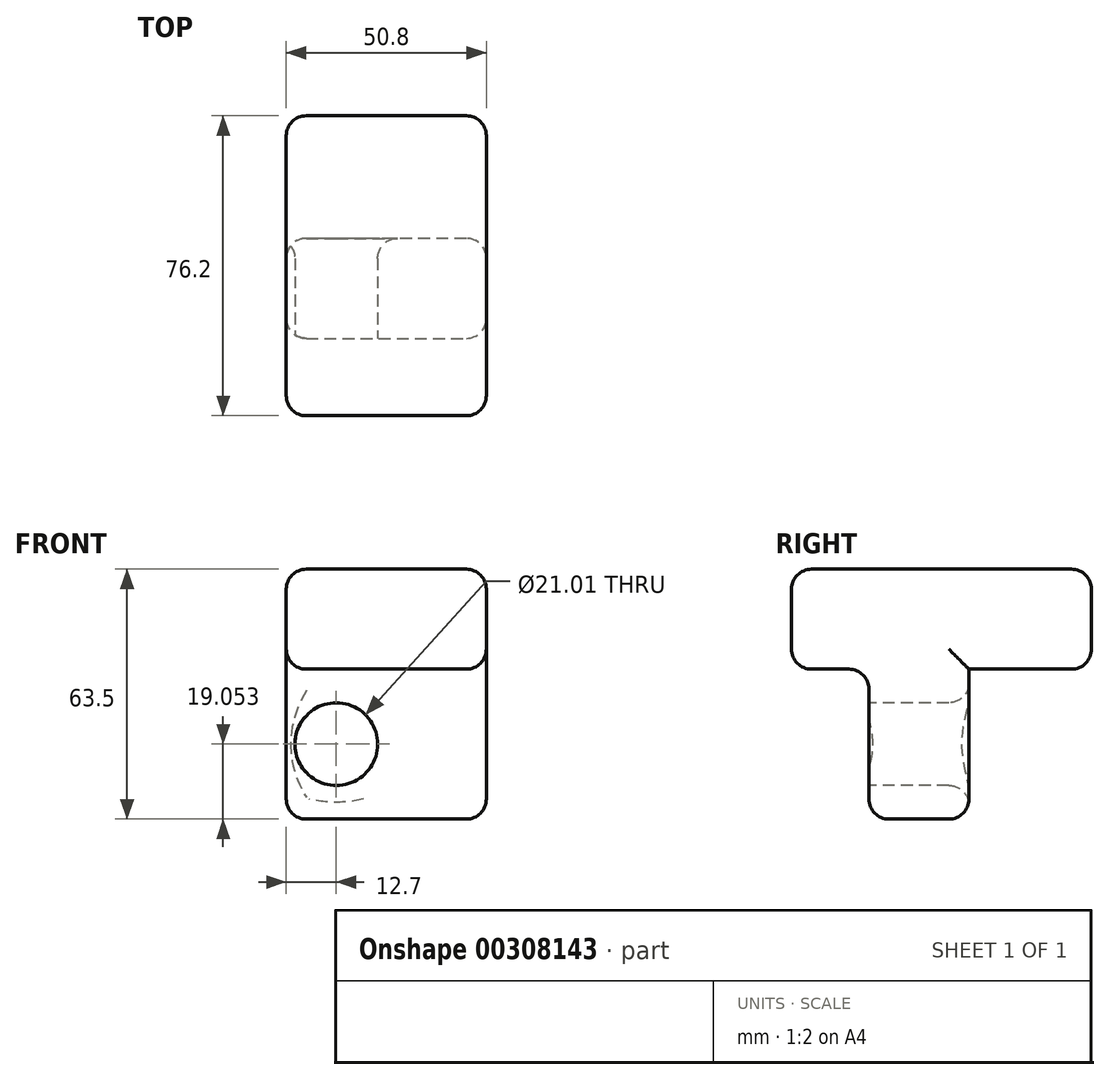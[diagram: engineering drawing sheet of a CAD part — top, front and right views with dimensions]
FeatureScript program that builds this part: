
annotation { "Feature Type Name" : "Feature", "Feature Type Description" : "" }
export const myFeature = defineFeature(function(context is Context, id is Id, definition is map)
    precondition{}
    {
        {
            var Q0;
            Q0=qCreatedBy(makeId("Front.planeOp"),FACE);
            var sketch = newSketch(context, id + "F0", { "sketchPlane" : qUnion([Q0])});
            skLineSegment(sketch, "E0", {"start": v(0, 47.5) * mm, "end": v(25.4, 47.5) * mm});
            skLineSegment(sketch, "E1", {"start": v(25.4, 47.5) * mm, "end": v(25.4, 22.1) * mm});
            skLineSegment(sketch, "E2", {"start": v(0, 22.1) * mm, "end": v(0, 47.5) * mm});
            skLineSegment(sketch, "E3", {"start": v(25.4, 22.1) * mm, "end": v(0, 22.1) * mm});
            skSolve(sketch);
        }
        {
            var Q0;
            Q0=makeQuery(id+"F0.imprint","IMPRINT",FACE,{"disambiguationData":[TD([[makeQuery(id+"F0.imprint","IMPRINT",EDGE,{"derivedFrom":sQuery(id+"F0.wireOp",EDGE,"E0")}),-1.0]])]});
            extrude(context, id + "F1", {"entities" : qUnion([Q0]), "depth" : 76.2 * mm});
        }
        {
            var Q0;
            Q0=makeQuery(id+"F1.opExtrude","SWEPT_FACE",FACE,{"disambiguationData":[OSD([sQuery(id+"F0.wireOp",EDGE,"E3")])]});
            var sketch = newSketch(context, id + "F2", { "sketchPlane" : qUnion([Q0])});
            skLineSegment(sketch, "E4", {"start": v(0, 56.54) * mm, "end": v(25.4, 56.54) * mm});
            skLineSegment(sketch, "E5", {"start": v(25.4, 56.54) * mm, "end": v(25.4, 31.14) * mm});
            skLineSegment(sketch, "E6", {"start": v(25.4, 31.14) * mm, "end": v(0, 31.14) * mm});
            skLineSegment(sketch, "E7", {"start": v(0, 31.14) * mm, "end": v(0, 56.54) * mm});
            skSolve(sketch);
        }
        {
            var Q0;
            Q0 = qSketchRegion(id + "F2", true);
            extrude(context, id + "F3", {"entities" : qUnion([Q0]), "operationType" : NewBodyOperationType.ADD, "depth" : 38.1 * mm});
        }
        {
            var Q0;
            Q0=makeQuery(id+"F3.opExtrude","SWEPT_FACE",FACE,{"disambiguationData":[OSD([sQuery(id+"F2.wireOp",EDGE,"E4")])]});
            var sketch = newSketch(context, id + "F4", { "sketchPlane" : qUnion([Q0])});
            skCircle(sketch, "E8", {"center": v(12.7, 3.04) * mm, "radius": 10.5 * mm});
            skPoint(sketch, "E8.centerSnap0", {"position": v(12.7, 22.1) * mm});
            skPoint(sketch, "E8.centerSnap1", {"position": v(0, 3.04) * mm});
            skSolve(sketch);
        }
        {
            var Q0;
            Q0=makeQuery(id+"F4.imprint","IMPRINT",FACE,{"disambiguationData":[TD([[makeQuery(id+"F4.imprint","IMPRINT",EDGE,{"derivedFrom":sQuery(id+"F4.wireOp",EDGE,"E8")}),1.0]])]});
            extrude(context, id + "F5", {"entities" : qUnion([Q0]), "operationType" : NewBodyOperationType.REMOVE, "endBound" : BoundingType.THROUGH_ALL, "oppositeDirection" : true, "depth" : 25.4 * mm});
        }
        {
            var Q0;
            Q0=makeQuery(id+"F3.boolean.opBoolean","MERGE",FACE,{"derivedFrom":[makeQuery(id+"F1.opExtrude","SWEPT_FACE",FACE,{"disambiguationData":[OSD([sQuery(id+"F0.wireOp",EDGE,"E1")])]}),makeQuery(id+"F3.opExtrude","SWEPT_FACE",FACE,{"disambiguationData":[OSD([sQuery(id+"F2.wireOp",EDGE,"E5")])]})]});
            var sketch = newSketch(context, id + "F6", { "sketchPlane" : qUnion([Q0])});
            skSolve(sketch);
        }
        {
            var Q0;
            {var subQ3=sQuery(id+"F0.wireOp",EDGE,"E1");Q0=makeQuery(id+"F6.imprint","IMPRINT",FACE,{"disambiguationData":[TD([[makeQuery(id+"F6.imprint","IMPRINT",EDGE,{"derivedFrom":makeQuery(id+"F1.opExtrude","CAP_EDGE",EDGE,{"disambiguationData":[OSD([subQ3])],"isStart":true})}),-1.0]])]});}
            extrude(context, id + "F7", {"entities" : qUnion([Q0]), "operationType" : NewBodyOperationType.ADD, "depth" : 25.4 * mm});
        }
        {
            var Q0;
            Q0=makeQuery(id+"F7.opExtrude","CAP_FACE",FACE,{"disambiguationData":[OSD([sQuery(id+"F0.wireOp",EDGE,"E0"),sQuery(id+"F0.wireOp",EDGE,"E1"),sQuery(id+"F0.wireOp",EDGE,"E3"),sQuery(id+"F2.wireOp",EDGE,"E4"),sQuery(id+"F2.wireOp",EDGE,"E5"),sQuery(id+"F2.wireOp",EDGE,"E6")])],"isStart":false});
            var Q1;
            {var subQ0=sQuery(id+"F2.wireOp",EDGE,"E5");var subQ1=sQuery(id+"F2.wireOp",EDGE,"E4");var subQ2=sQuery(id+"F0.wireOp",EDGE,"E3");var subQ3=sQuery(id+"F0.wireOp",EDGE,"E1");Q1=makeQuery(id+"F7.boolean.opBoolean","MERGE",EDGE,{"derivedFrom":[makeQuery(id+"F3.opExtrude","CAP_EDGE",EDGE,{"disambiguationData":[OSD([subQ1])],"isStart":false}),makeQuery(id+"F7.opExtrude","SWEPT_EDGE",EDGE,{"disambiguationData":[OSD([subQ3,subQ2,subQ1,subQ0]),TDD([makeQuery(id+"F6.imprint","INTERSECT",VERTEX,{"derivedFrom":[makeQuery(id+"F3.opExtrude","SWEPT_EDGE",EDGE,{"disambiguationData":[OSD([subQ3,subQ2,subQ1,subQ0])]}),makeQuery(id+"F3.opExtrude","CAP_EDGE",EDGE,{"disambiguationData":[OSD([subQ0])],"isStart":false})]})])]})]});}
            var Q2;
            {var subQ0=sQuery(id+"F2.wireOp",EDGE,"E5");var subQ1=sQuery(id+"F2.wireOp",EDGE,"E6");var subQ2=sQuery(id+"F0.wireOp",EDGE,"E3");var subQ3=sQuery(id+"F0.wireOp",EDGE,"E1");Q2=makeQuery(id+"F7.boolean.opBoolean","MERGE",EDGE,{"derivedFrom":[makeQuery(id+"F3.opExtrude","CAP_EDGE",EDGE,{"disambiguationData":[OSD([subQ1])],"isStart":false}),makeQuery(id+"F7.opExtrude","SWEPT_EDGE",EDGE,{"disambiguationData":[OSD([subQ3,subQ2,subQ0,subQ1]),TDD([makeQuery(id+"F6.imprint","INTERSECT",VERTEX,{"derivedFrom":[makeQuery(id+"F3.opExtrude","SWEPT_EDGE",EDGE,{"disambiguationData":[OSD([subQ3,subQ2,subQ0,subQ1])]}),makeQuery(id+"F3.opExtrude","CAP_EDGE",EDGE,{"disambiguationData":[OSD([subQ0])],"isStart":false})]})])]})]});}
            var Q3;
            {var subQ0=sQuery(id+"F2.wireOp",EDGE,"E4");var subQ1=sQuery(id+"F0.wireOp",EDGE,"E3");var subQ2=sQuery(id+"F0.wireOp",EDGE,"E1");var subQ3=sQuery(id+"F2.wireOp",EDGE,"E5");Q3=makeQuery(id+"F7.boolean.opBoolean","MERGE",EDGE,{"derivedFrom":[makeQuery(id+"F3.opExtrude","CAP_EDGE",EDGE,{"disambiguationData":[OSD([subQ0])],"isStart":true}),makeQuery(id+"F7.opExtrude","SWEPT_EDGE",EDGE,{"disambiguationData":[OSD([subQ2,subQ1,subQ0,subQ3]),TDD([makeQuery(id+"F6.imprint","INTERSECT",VERTEX,{"derivedFrom":[makeQuery(id+"F3.opExtrude","SWEPT_EDGE",EDGE,{"disambiguationData":[OSD([subQ2,subQ1,subQ0,subQ3])]}),makeQuery(id+"F3.boolean.opBoolean","SPLIT",EDGE,{"disambiguationData":[TD([makeQuery(id+"F3.opExtrude","SWEPT_FACE",FACE,{"disambiguationData":[OSD([subQ0])]})])],"derivedFrom":makeQuery(id+"F1.opExtrude","SWEPT_EDGE",EDGE,{"disambiguationData":[OSD([subQ2,subQ1])]})})]})])]})]});}
            var Q4;
            {var subQ0=sQuery(id+"F0.wireOp",EDGE,"E3");var subQ1=sQuery(id+"F0.wireOp",EDGE,"E1");Q4=makeQuery(id+"F7.boolean.opBoolean","MERGE",EDGE,{"derivedFrom":[makeQuery(id+"F1.opExtrude","CAP_EDGE",EDGE,{"disambiguationData":[OSD([subQ0])],"isStart":false}),makeQuery(id+"F7.opExtrude","SWEPT_EDGE",EDGE,{"disambiguationData":[OSD([subQ1,subQ0]),TDD([makeQuery(id+"F6.imprint","INTERSECT",VERTEX,{"derivedFrom":[makeQuery(id+"F1.opExtrude","CAP_EDGE",EDGE,{"disambiguationData":[OSD([subQ1])],"isStart":false}),makeQuery(id+"F3.boolean.opBoolean","SPLIT",EDGE,{"disambiguationData":[TD([makeQuery(id+"F3.opExtrude","SWEPT_FACE",FACE,{"disambiguationData":[OSD([sQuery(id+"F2.wireOp",EDGE,"E4")])]})])],"derivedFrom":makeQuery(id+"F1.opExtrude","SWEPT_EDGE",EDGE,{"disambiguationData":[OSD([subQ1,subQ0])]})})]})])]})]});}
            var Q5;
            Q5=makeQuery(id+"F5.boolean.opBoolean","INTERSECT",EDGE,{"derivedFrom":[makeQuery(id+"F3.opExtrude","SWEPT_FACE",FACE,{"disambiguationData":[OSD([sQuery(id+"F2.wireOp",EDGE,"E6")])]}),makeQuery(id+"F5.opExtrude","SWEPT_FACE",FACE,{"disambiguationData":[OSD([sQuery(id+"F4.wireOp",EDGE,"E8")])]})]});
            var Q6;
            {var subQ0=sQuery(id+"F0.wireOp",EDGE,"E3");var subQ1=sQuery(id+"F0.wireOp",EDGE,"E1");Q6=makeQuery(id+"F7.boolean.opBoolean","MERGE",EDGE,{"derivedFrom":[makeQuery(id+"F1.opExtrude","CAP_EDGE",EDGE,{"disambiguationData":[OSD([subQ0])],"isStart":true}),makeQuery(id+"F7.opExtrude","SWEPT_EDGE",EDGE,{"disambiguationData":[OSD([subQ1,subQ0]),TDD([makeQuery(id+"F6.imprint","INTERSECT",VERTEX,{"derivedFrom":[makeQuery(id+"F1.opExtrude","CAP_EDGE",EDGE,{"disambiguationData":[OSD([subQ1])],"isStart":true}),makeQuery(id+"F3.boolean.opBoolean","SPLIT",EDGE,{"disambiguationData":[TD([makeQuery(id+"F3.opExtrude","SWEPT_FACE",FACE,{"disambiguationData":[OSD([sQuery(id+"F2.wireOp",EDGE,"E6")])]})])],"derivedFrom":makeQuery(id+"F1.opExtrude","SWEPT_EDGE",EDGE,{"disambiguationData":[OSD([subQ1,subQ0])]})})]})])]})]});}
            var Q7;
            Q7=makeQuery(id+"F3.boolean.opBoolean","MERGE",FACE,{"derivedFrom":[makeQuery(id+"F1.opExtrude","SWEPT_FACE",FACE,{"disambiguationData":[OSD([sQuery(id+"F0.wireOp",EDGE,"E2")])]}),makeQuery(id+"F3.opExtrude","SWEPT_FACE",FACE,{"disambiguationData":[OSD([sQuery(id+"F2.wireOp",EDGE,"E7")])]})]});
            var Q8;
            {var subQ0=sQuery(id+"F0.wireOp",EDGE,"E0");Q8=makeQuery(id+"F7.boolean.opBoolean","MERGE",FACE,{"derivedFrom":[makeQuery(id+"F1.opExtrude","SWEPT_FACE",FACE,{"disambiguationData":[OSD([subQ0])]}),makeQuery(id+"F7.opExtrude","SWEPT_FACE",FACE,{"disambiguationData":[OSD([subQ0,sQuery(id+"F0.wireOp",EDGE,"E1")])]})]});}
            fillet(context, id + "F8", {"entities" : qUnion([Q0, Q1, Q2, Q3, Q4, Q5, Q6, Q7, Q8]), "radius" : 5.08 * mm, "tangentPropagation" : true, "allowEdgeOverflow" : false});
        }
    });
